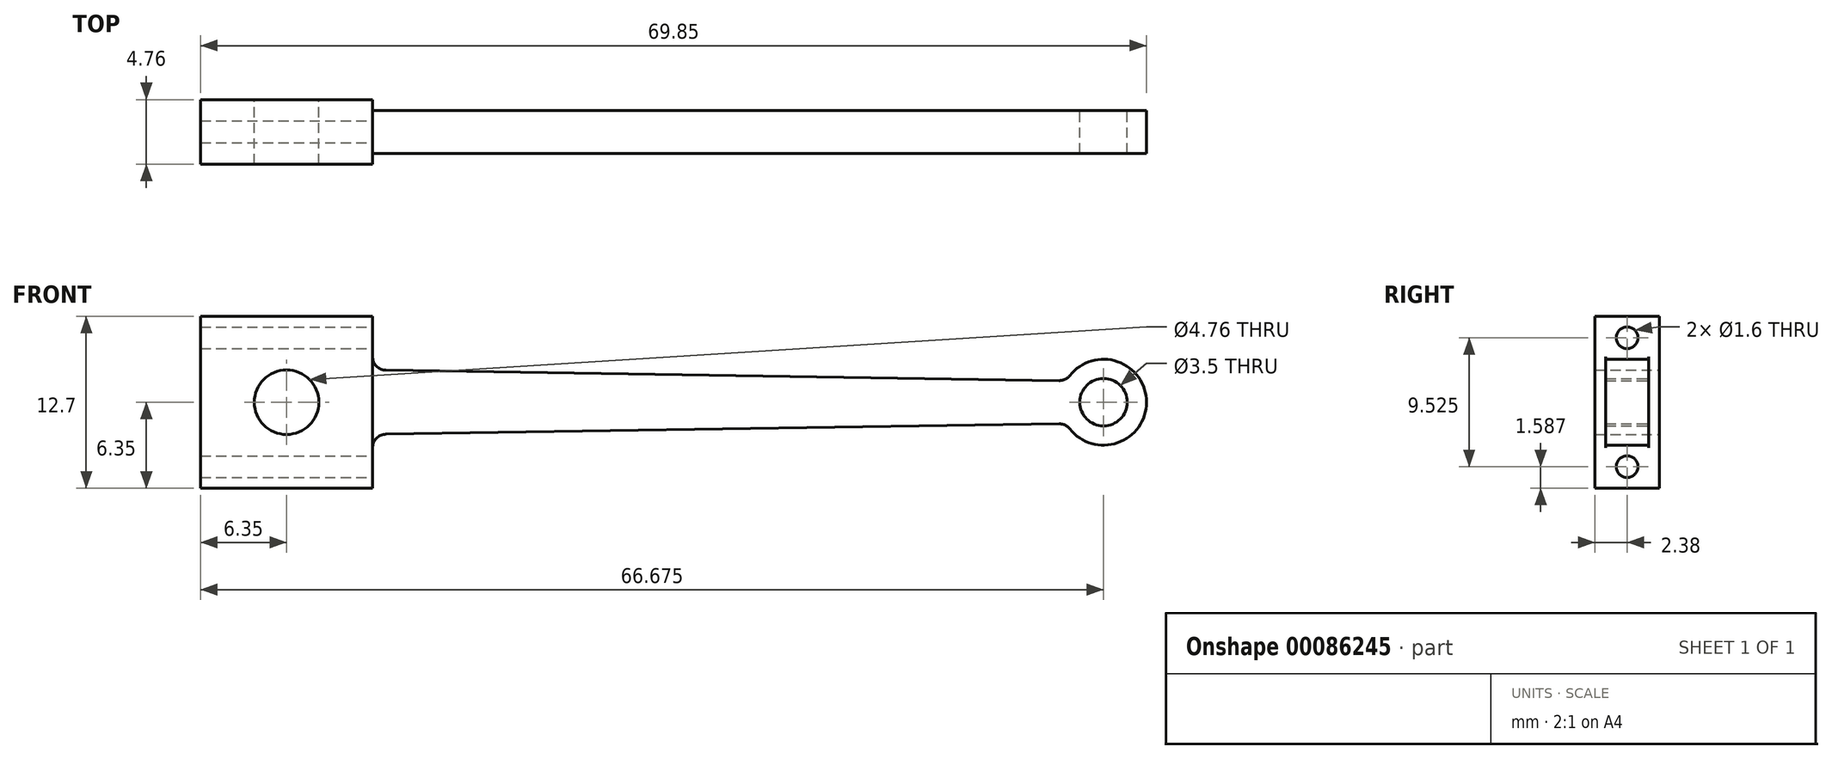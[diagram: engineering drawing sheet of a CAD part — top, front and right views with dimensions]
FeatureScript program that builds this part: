
annotation { "Feature Type Name" : "Feature", "Feature Type Description" : "" }
export const myFeature = defineFeature(function(context is Context, id is Id, definition is map)
    precondition{}
    {
        {
            var Q0;
            Q0=qCreatedBy(makeId("Front.planeOp"),FACE);
            var sketch = newSketch(context, id + "F0", { "sketchPlane" : qUnion([Q0])});
            skCircle(sketch, "E0", {"center": v(0, 0) * mm, "radius": 2.38 * mm});
            skCircle(sketch, "E1", {"center": v(60.32, 0) * mm, "radius": 1.75 * mm});
            skArc(sketch, "E2", {"start": v(57.58, -1.59) * mm, "mid": v(63.5, 0) * mm, "end": v(57.58, 1.59) * mm});
            skLineSegment(sketch, "E3.bottom", {"start": v(6.35, 6.35) * mm, "end": v(-6.35, 6.35) * mm});
            skLineSegment(sketch, "E3.top", {"start": v(6.35, -6.35) * mm, "end": v(-6.35, -6.35) * mm});
            skLineSegment(sketch, "E3.left", {"start": v(6.35, 6.35) * mm, "end": v(6.35, 2.38) * mm});
            skLineSegment(sketch, "E3.right", {"start": v(-6.35, 6.35) * mm, "end": v(-6.35, -6.35) * mm});
            skLineSegment(sketch, "E4", {"start": v(60.32, 0) * mm, "end": v(0, 0) * mm, "construction": true});
            skLineSegment(sketch, "E5", {"start": v(57.58, 1.59) * mm, "end": v(6.35, 2.38) * mm});
            skLineSegment(sketch, "E6", {"start": v(57.58, -1.59) * mm, "end": v(6.35, -2.38) * mm});
            skLineSegment(sketch, "E7.trimOffspring", {"start": v(6.35, -2.38) * mm, "end": v(6.35, -6.35) * mm});
            skSolve(sketch);
        }
        {
            var Q0;
            Q0=makeQuery(id+"F0.imprint","IMPRINT",FACE,{"disambiguationData":[TD([[makeQuery(id+"F0.imprint","IMPRINT",EDGE,{"derivedFrom":sQuery(id+"F0.wireOp",EDGE,"E0")}),-1.0]])]});
            extrude(context, id + "F1", {"entities" : qUnion([Q0]), "depth" : ((3 / 16) * 25.4) * mm, "symmetric" : true});
        }
        {
            var Q0;
            Q0=qCreatedBy(makeId("Top.planeOp"),FACE);
            var sketch = newSketch(context, id + "F2", { "sketchPlane" : qUnion([Q0])});
            skLineSegment(sketch, "E8.bottom", {"start": v(6.35, 2.38) * mm, "end": v(63.5, 2.38) * mm});
            skLineSegment(sketch, "E8.top", {"start": v(6.35, 1.59) * mm, "end": v(63.5, 1.59) * mm});
            skLineSegment(sketch, "E8.left", {"start": v(6.35, 2.38) * mm, "end": v(6.35, 1.59) * mm});
            skLineSegment(sketch, "E8.right", {"start": v(63.5, 2.38) * mm, "end": v(63.5, 1.59) * mm});
            skLineSegment(sketch, "E9.bottom", {"start": v(6.35, -1.59) * mm, "end": v(63.5, -1.59) * mm});
            skLineSegment(sketch, "E9.top", {"start": v(6.35, -2.38) * mm, "end": v(63.5, -2.38) * mm});
            skLineSegment(sketch, "E9.left", {"start": v(6.35, -1.59) * mm, "end": v(6.35, -2.38) * mm});
            skLineSegment(sketch, "E9.right", {"start": v(63.5, -1.59) * mm, "end": v(63.5, -2.38) * mm});
            skLineSegment(sketch, "E10", {"start": v(0, 0) * mm, "end": v(126.94, 0) * mm, "construction": true});
            skSolve(sketch);
        }
        {
            var Q0;
            Q0 = qSketchRegion(id + "F2", true);
            extrude(context, id + "F3", {"entities" : qUnion([Q0]), "operationType" : NewBodyOperationType.REMOVE, "depth" : 25 * mm, "symmetric" : true});
        }
        {
            var Q0;
            Q0=makeQuery(id+"F1.opExtrude","SWEPT_FACE",FACE,{"disambiguationData":[OSD([sQuery(id+"F0.wireOp",EDGE,"E3.right")])]});
            var sketch = newSketch(context, id + "F4", { "sketchPlane" : qUnion([Q0])});
            skPoint(sketch, "E11", {"position": v(0, 4.76) * mm});
            skPoint(sketch, "E12", {"position": v(0, -4.76) * mm});
            skLineSegment(sketch, "E13", {"start": v(0, 0) * mm, "end": v(18.67, 0) * mm, "construction": true});
            skSolve(sketch);
        }
        {
            var Q0;
            Q0=sQuery(id+"F4.wireOp",VERTEX,"E11");
            var Q1;
            Q1=sQuery(id+"F4.wireOp",VERTEX,"E12");
            var Q2;
            Q2=makeQuery(id+"F1.opExtrude","SWEPT_BODY",BODY,{"disambiguationData":[OSD([sQuery(id+"F0.wireOp",EDGE,"E0"),sQuery(id+"F0.wireOp",EDGE,"E1"),sQuery(id+"F0.wireOp",EDGE,"E2"),sQuery(id+"F0.wireOp",EDGE,"E3.bottom"),sQuery(id+"F0.wireOp",EDGE,"E3.top"),sQuery(id+"F0.wireOp",EDGE,"E3.left"),sQuery(id+"F0.wireOp",EDGE,"E3.right"),sQuery(id+"F0.wireOp",EDGE,"E5"),sQuery(id+"F0.wireOp",EDGE,"E6"),sQuery(id+"F0.wireOp",EDGE,"E7.trimOffspring")])]});
            hole(context, id + "F5", {"style" : HoleStyle.SIMPLE, "endStyle" : HoleEndStyle.THROUGH, "holeDiameter" : 1.6 * mm, "locations" : qUnion([Q0, Q1]), "scope" : qUnion([Q2]), "isTappedThrough" : true});
        }
        {
            var Q0;
            Q0=makeQuery(id+"F1.opExtrude","SWEPT_EDGE",EDGE,{"disambiguationData":[OSD([sQuery(id+"F0.wireOp",EDGE,"E3.left"),sQuery(id+"F0.wireOp",EDGE,"E5")])]});
            var Q1;
            Q1=makeQuery(id+"F1.opExtrude","SWEPT_EDGE",EDGE,{"disambiguationData":[OSD([sQuery(id+"F0.wireOp",EDGE,"E6"),sQuery(id+"F0.wireOp",EDGE,"E7.trimOffspring")])]});
            var Q2;
            Q2=makeQuery(id+"F1.opExtrude","SWEPT_EDGE",EDGE,{"disambiguationData":[OSD([sQuery(id+"F0.wireOp",EDGE,"E2"),sQuery(id+"F0.wireOp",EDGE,"E5")])]});
            var Q3;
            Q3=makeQuery(id+"F1.opExtrude","SWEPT_EDGE",EDGE,{"disambiguationData":[OSD([sQuery(id+"F0.wireOp",EDGE,"E2"),sQuery(id+"F0.wireOp",EDGE,"E6")])]});
            fillet(context, id + "F6", {"entities" : qUnion([Q0, Q1, Q2, Q3]), "radius" : 1 * mm, "tangentPropagation" : true, "allowEdgeOverflow" : false});
        }
    });
